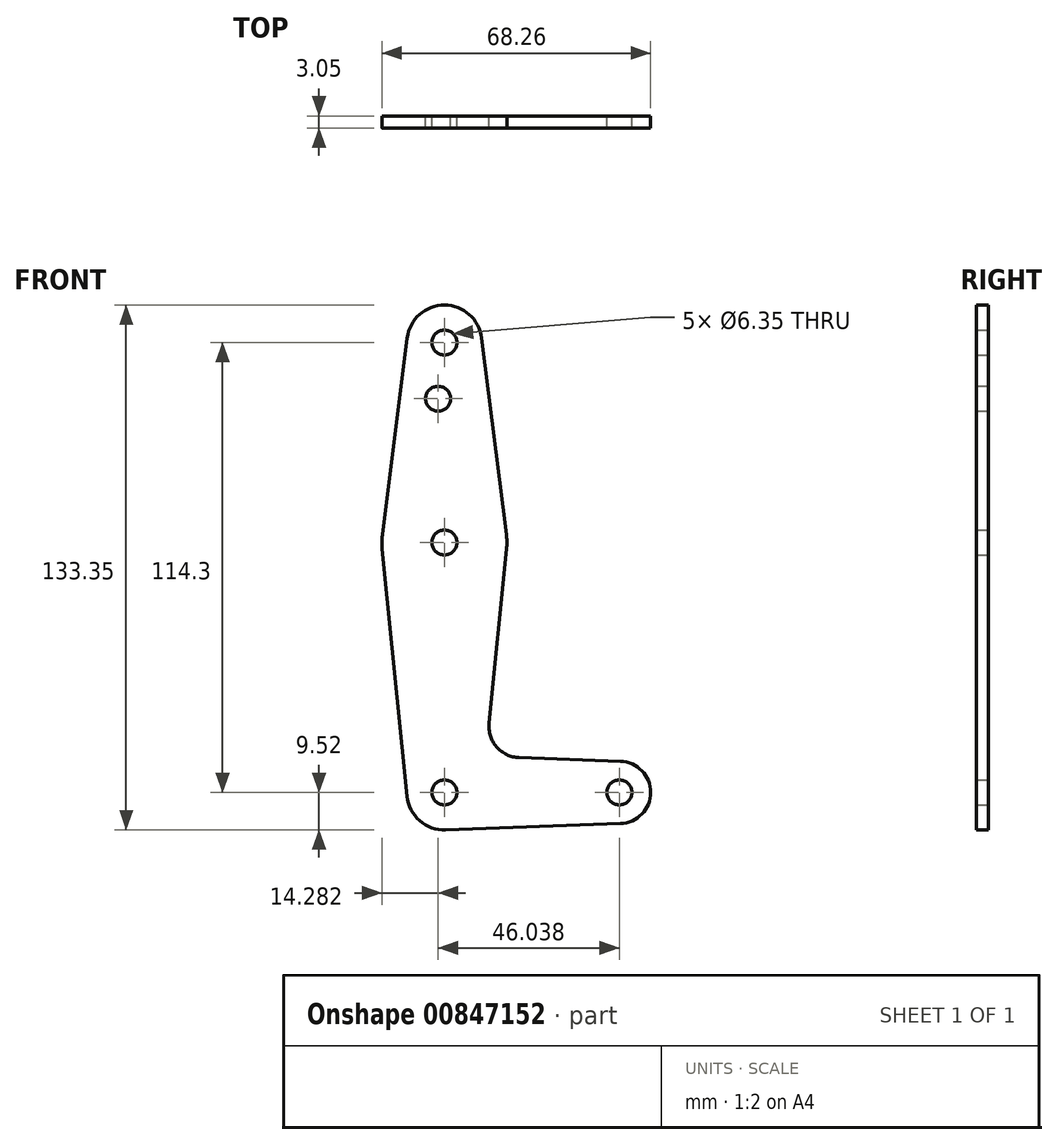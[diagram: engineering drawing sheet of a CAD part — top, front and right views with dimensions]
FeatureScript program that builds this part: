
annotation { "Feature Type Name" : "Feature", "Feature Type Description" : "" }
export const myFeature = defineFeature(function(context is Context, id is Id, definition is map)
    precondition{}
    {
        {
            var Q0;
            Q0=qCreatedBy(makeId("Front.planeOp"),FACE);
            var sketch = newSketch(context, id + "F0", { "sketchPlane" : qUnion([Q0])});
            skCircle(sketch, "E0", {"center": v(0, 0) * mm, "radius": 9.53 * mm});
            skCircle(sketch, "E1", {"center": v(0, 63.5) * mm, "radius": 15.88 * mm});
            skCircle(sketch, "E2", {"center": v(0, 114.3) * mm, "radius": 9.53 * mm});
            skCircle(sketch, "E3", {"center": v(44.45, 0) * mm, "radius": 7.94 * mm});
            skLineSegment(sketch, "E4", {"start": v(0, 0) * mm, "end": v(0, 114.3) * mm, "construction": true});
            skLineSegment(sketch, "E5", {"start": v(0, 0) * mm, "end": v(44.45, 0) * mm, "construction": true});
            skLineSegment(sketch, "E6", {"start": v(18.97, 8.85) * mm, "end": v(44.73, 7.93) * mm});
            skLineSegment(sketch, "E7", {"start": v(0.34, -9.52) * mm, "end": v(44.73, -7.93) * mm});
            skLineSegment(sketch, "E8", {"start": v(-15.8, 61.91) * mm, "end": v(-9.48, -0.95) * mm});
            skLineSegment(sketch, "E9", {"start": v(15.8, 61.91) * mm, "end": v(11.34, 17.6) * mm});
            skLineSegment(sketch, "E10", {"start": v(-9.45, 115.5) * mm, "end": v(-15.75, 65.48) * mm});
            skLineSegment(sketch, "E11", {"start": v(9.45, 115.5) * mm, "end": v(15.75, 65.48) * mm});
            skCircle(sketch, "E12", {"center": v(0, 114.3) * mm, "radius": 3.18 * mm});
            skCircle(sketch, "E13", {"center": v(0, 63.5) * mm, "radius": 3.18 * mm});
            skCircle(sketch, "E14", {"center": v(0, 0) * mm, "radius": 3.18 * mm});
            skCircle(sketch, "E15", {"center": v(44.45, 0) * mm, "radius": 3.18 * mm});
            skCircle(sketch, "E16", {"center": v(-1.59, 100.03) * mm, "radius": 3.18 * mm});
            skArc(sketch, "E17.filletArc", {"start": v(11.34, 17.6) * mm, "mid": v(13.26, 11.57) * mm, "end": v(18.97, 8.85) * mm});
            skSolve(sketch);
        }
        {
            var Q0;
            Q0 = qSketchRegion(id + "F0", true);
            extrude(context, id + "F1", {"entities" : qUnion([Q0]), "depth" : 3.05 * mm, "offsetDistance" : 25.4 * mm});
        }
    });
